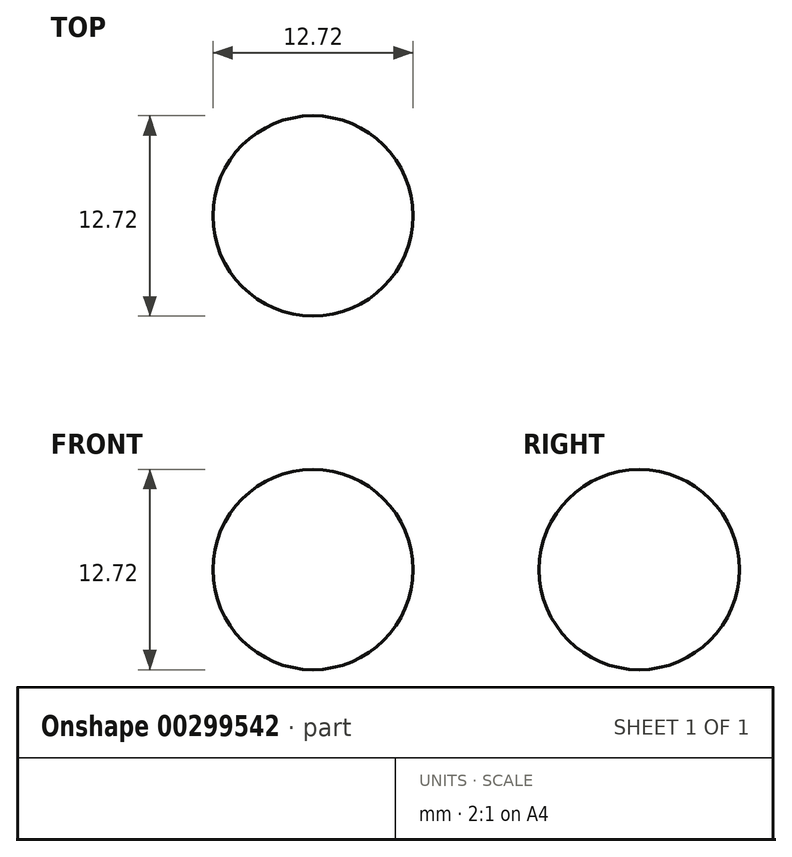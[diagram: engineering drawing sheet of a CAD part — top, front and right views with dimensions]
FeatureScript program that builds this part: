
annotation { "Feature Type Name" : "Feature", "Feature Type Description" : "" }
export const myFeature = defineFeature(function(context is Context, id is Id, definition is map)
    precondition{}
    {
        {
            var Q0;
            Q0=qCreatedBy(makeId("Front.planeOp"),FACE);
            var sketch = newSketch(context, id + "F0", { "sketchPlane" : qUnion([Q0])});
            skCircle(sketch, "E0", {"center": v(0, 0) * mm, "radius": 6.36 * mm});
            skLineSegment(sketch, "E1", {"start": v(0, 0) * mm, "end": v(0, 6.36) * mm});
            skLineSegment(sketch, "E2", {"start": v(0, 6.36) * mm, "end": v(0, -6.36) * mm});
            skSolve(sketch);
        }
        {
            var Q0;
            {var subQ0=sQuery(id+"F0.wireOp",EDGE,"E2");var subQ4=makeQuery(id+"F0.imprint","IMPRINT",VERTEX,{"derivedFrom":subQ0});Q0=makeQuery(id+"F0.imprint","IMPRINT",FACE,{"disambiguationData":[TD([[makeQuery(id+"F0.imprint","IMPRINT",EDGE,{"disambiguationData":[TD([[subQ4,1.0]])],"derivedFrom":subQ0}),1.0]])]});}
            var Q1;
            Q1=sQuery(id+"F0.wireOp",EDGE,"E2");
            revolve(context, id + "F1", {"entities" : qUnion([Q0]), "axis" : qUnion([Q1]), "revolveType" : RevolveType.FULL});
        }
    });
